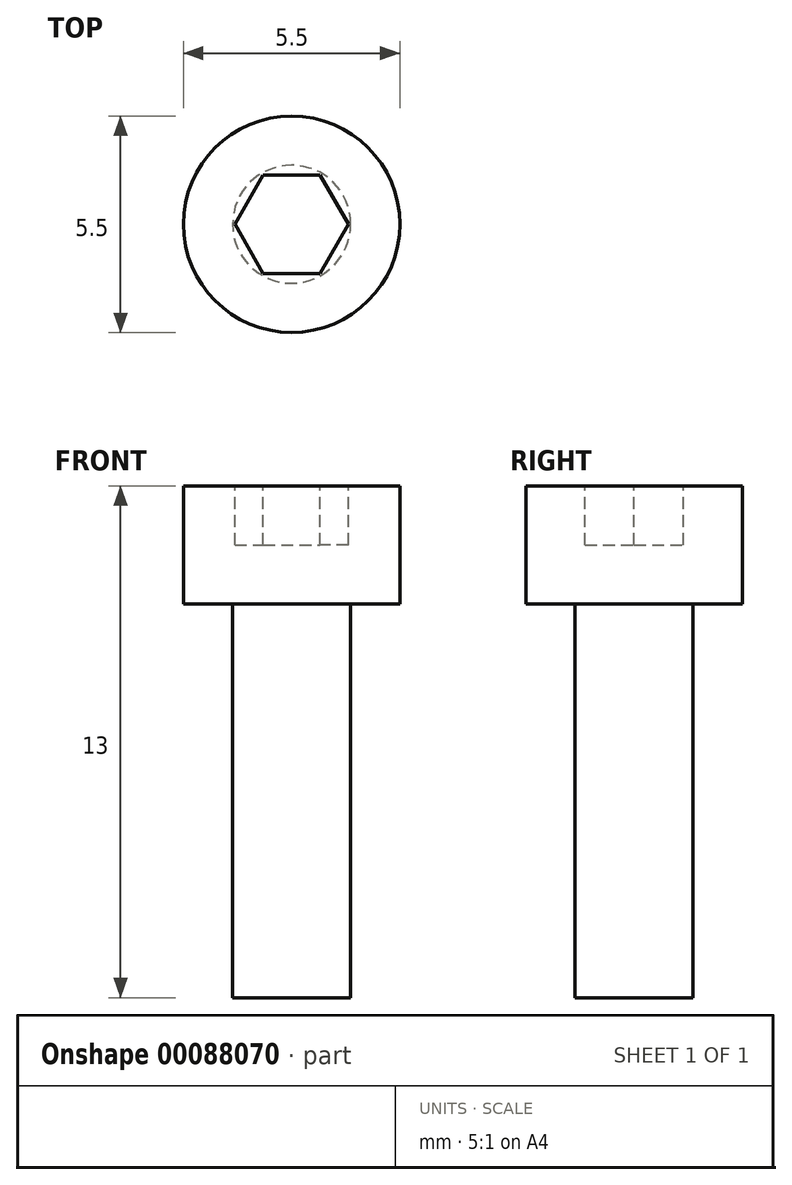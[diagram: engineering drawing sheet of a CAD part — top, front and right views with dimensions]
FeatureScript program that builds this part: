
annotation { "Feature Type Name" : "Feature", "Feature Type Description" : "" }
export const myFeature = defineFeature(function(context is Context, id is Id, definition is map)
    precondition{}
    {
        {
            var Q0;
            Q0=qCreatedBy(makeId("Front.planeOp"),FACE);
            var sketch = newSketch(context, id + "F0", { "sketchPlane" : qUnion([Q0])});
            skLineSegment(sketch, "E0", {"start": v(0, 0) * mm, "end": v(-2.75, 0) * mm});
            skLineSegment(sketch, "E1", {"start": v(-2.75, 0) * mm, "end": v(-2.75, -3) * mm});
            skLineSegment(sketch, "E2", {"start": v(-2.75, -3) * mm, "end": v(-1.5, -3) * mm});
            skLineSegment(sketch, "E3", {"start": v(-1.5, -3) * mm, "end": v(-1.5, -13) * mm});
            skLineSegment(sketch, "E4", {"start": v(-1.5, -13) * mm, "end": v(0, -13) * mm});
            skLineSegment(sketch, "E5", {"start": v(0, -13) * mm, "end": v(0, 0) * mm});
            skLineSegment(sketch, "E6", {"start": v(0, -9.74) * mm, "end": v(0, -13) * mm, "construction": true});
            skSolve(sketch);
        }
        {
            var Q0;
            Q0=makeQuery(id+"F0.imprint","IMPRINT",FACE,{"disambiguationData":[TD([[makeQuery(id+"F0.imprint","IMPRINT",EDGE,{"derivedFrom":sQuery(id+"F0.wireOp",EDGE,"E0")}),1.0]])]});
            var Q1;
            Q1=sQuery(id+"F0.wireOp",EDGE,"E5");
            revolve(context, id + "F1", {"entities" : qUnion([Q0]), "axis" : qUnion([Q1]), "revolveType" : RevolveType.FULL});
        }
        {
            var Q0;
            Q0=makeQuery(id+"F1.opRevolve","SWEPT_FACE",FACE,{"disambiguationData":[OSD([sQuery(id+"F0.wireOp",EDGE,"E0")])]});
            var sketch = newSketch(context, id + "F2", { "sketchPlane" : qUnion([Q0])});
            skCircle(sketch, "E7.cCircle", {"center": v(0, 0) * mm, "radius": 1.25 * mm, "construction": true});
            skLineSegment(sketch, "E7.0", {"start": v(-0.72, 1.25) * mm, "end": v(0.72, 1.25) * mm});
            skLineSegment(sketch, "E7.1", {"start": v(0.72, 1.25) * mm, "end": v(1.44, 0) * mm});
            skLineSegment(sketch, "E7.2", {"start": v(1.44, 0) * mm, "end": v(0.72, -1.25) * mm});
            skLineSegment(sketch, "E7.3", {"start": v(0.72, -1.25) * mm, "end": v(-0.72, -1.25) * mm});
            skLineSegment(sketch, "E7.4", {"start": v(-0.72, -1.25) * mm, "end": v(-1.44, 0) * mm});
            skLineSegment(sketch, "E7.5", {"start": v(-1.44, 0) * mm, "end": v(-0.72, 1.25) * mm});
            skPoint(sketch, "E7.0.midPoint", {"position": v(0, 1.25) * mm});
            skSolve(sketch);
        }
        {
            var Q0;
            Q0=makeQuery(id+"F2.imprint","IMPRINT",FACE,{"disambiguationData":[TD([[makeQuery(id+"F2.imprint","IMPRINT",EDGE,{"derivedFrom":sQuery(id+"F2.wireOp",EDGE,"E7.0")}),-1.0]])]});
            extrude(context, id + "F3", {"entities" : qUnion([Q0]), "operationType" : NewBodyOperationType.REMOVE, "oppositeDirection" : true, "depth" : 1.5 * mm});
        }
    });
